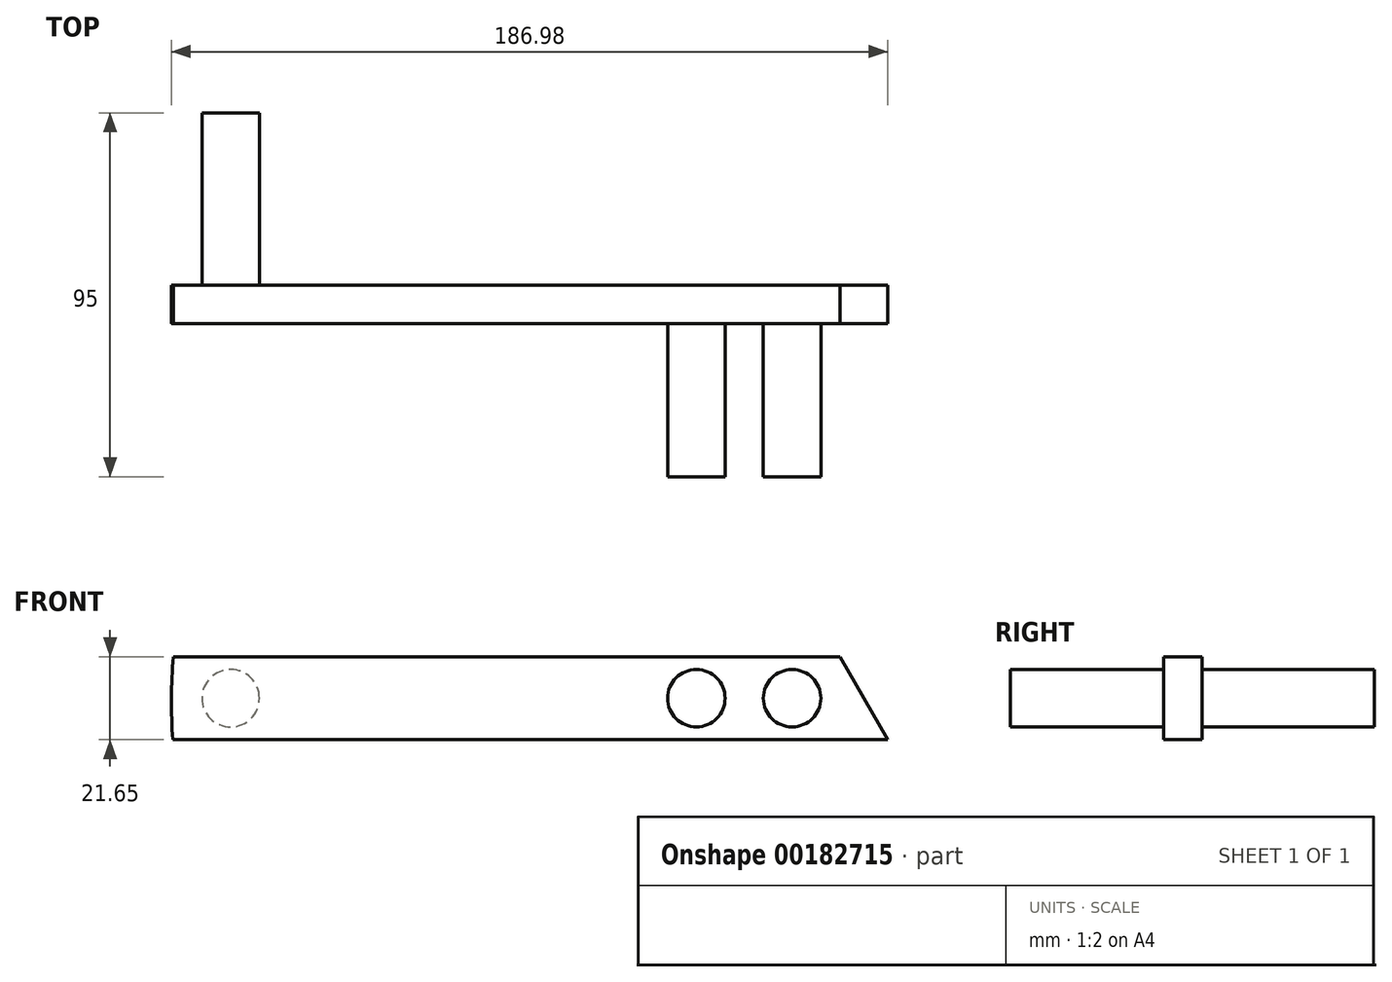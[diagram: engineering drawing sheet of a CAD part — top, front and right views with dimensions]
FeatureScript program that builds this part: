
annotation { "Feature Type Name" : "Feature", "Feature Type Description" : "" }
export const myFeature = defineFeature(function(context is Context, id is Id, definition is map)
    precondition{}
    {
        {
            var Q0;
            Q0=qCreatedBy(makeId("Front.planeOp"),FACE);
            var sketch = newSketch(context, id + "F0", { "sketchPlane" : qUnion([Q0])});
            skLineSegment(sketch, "E0", {"start": v(-38.02, -9.92) * mm, "end": v(-25.52, 11.73) * mm});
            skLineSegment(sketch, "E1", {"start": v(24.48, 11.73) * mm, "end": v(-25.52, 11.73) * mm});
            skLineSegment(sketch, "E2", {"start": v(36.98, -9.92) * mm, "end": v(24.48, 11.73) * mm});
            skLineSegment(sketch, "E3", {"start": v(36.98, -9.92) * mm, "end": v(-13.02, -9.92) * mm});
            skLineSegment(sketch, "E4", {"start": v(36.98, -9.92) * mm, "end": v(-38.02, -9.92) * mm});
            skLineSegment(sketch, "E5", {"start": v(11.98, -9.92) * mm, "end": v(11.98, -9.46) * mm});
            skLineSegment(sketch, "E6.trimOffspring", {"start": v(11.98, 11.26) * mm, "end": v(11.98, 11.73) * mm});
            skPoint(sketch, "E7", {"position": v(11.98, 0.9) * mm});
            skPoint(sketch, "E8", {"position": v(-13.02, 0.9) * mm});
            skPoint(sketch, "E9.orphan", {"position": v(-31.77, 0.9) * mm});
            skPoint(sketch, "E10.orphan", {"position": v(-13.02, 11.73) * mm});
            skCircle(sketch, "E11", {"center": v(-13.02, 0.9) * mm, "radius": 7.5 * mm});
            skCircle(sketch, "E12", {"center": v(11.98, 0.9) * mm, "radius": 7.5 * mm});
            skLineSegment(sketch, "E13", {"start": v(0, 0) * mm, "end": v(0, -9.92) * mm});
            skPoint(sketch, "E14", {"position": v(0, -9.92) * mm});
            skCircle(sketch, "E15", {"center": v(0, 0) * mm, "radius": 120 * mm});
            skLineSegment(sketch, "E16", {"start": v(36.98, -9.92) * mm, "end": v(-119.59, -9.92) * mm});
            skLineSegment(sketch, "E17", {"start": v(24.48, 11.73) * mm, "end": v(-119.43, 11.73) * mm});
            skCircle(sketch, "E18", {"center": v(0, 0) * mm, "radius": 150 * mm});
            skLineSegment(sketch, "E19", {"start": v(-119.43, 11.73) * mm, "end": v(-149.54, 11.73) * mm});
            skLineSegment(sketch, "E20", {"start": v(-119.59, -9.92) * mm, "end": v(-149.67, -9.92) * mm});
            skPoint(sketch, "E21", {"position": v(-134.56, 0.9) * mm});
            skCircle(sketch, "E22", {"center": v(-134.56, 0.9) * mm, "radius": 7.5 * mm});
            skSolve(sketch);
        }
        {
            var Q0;
            {var subQ2=sQuery(id+"F0.wireOp",EDGE,"E0");Q0=makeQuery(id+"F0.imprint","IMPRINT",FACE,{"disambiguationData":[TD([[makeQuery(id+"F0.imprint","IMPRINT",EDGE,{"derivedFrom":subQ2}),-1.0]])]});}
            var Q1;
            {var subQ0=sQuery(id+"F0.wireOp",EDGE,"E0");Q1=makeQuery(id+"F0.imprint","IMPRINT",FACE,{"disambiguationData":[TD([[makeQuery(id+"F0.imprint","IMPRINT",EDGE,{"derivedFrom":subQ0}),1.0]])]});}
            var Q2;
            {var subQ2=sQuery(id+"F0.wireOp",EDGE,"E19");Q2=makeQuery(id+"F0.imprint","IMPRINT",FACE,{"disambiguationData":[TD([[makeQuery(id+"F0.imprint","IMPRINT",EDGE,{"derivedFrom":subQ2}),1.0]])]});}
            var Q3;
            Q3=makeQuery(id+"F0.imprint","IMPRINT",FACE,{"disambiguationData":[TD([[makeQuery(id+"F0.imprint","IMPRINT",EDGE,{"derivedFrom":sQuery(id+"F0.wireOp",EDGE,"E22")}),1.0]])]});
            extrude(context, id + "F1", {"entities" : qUnion([Q0, Q1, Q2, Q3]), "depth" : 10 * mm});
        }
        {
            var Q0;
            Q0=makeQuery(id+"F0.imprint","IMPRINT",FACE,{"disambiguationData":[TD([[makeQuery(id+"F0.imprint","IMPRINT",EDGE,{"derivedFrom":sQuery(id+"F0.wireOp",EDGE,"E11")}),1.0]])]});
            var Q1;
            Q1=makeQuery(id+"F0.imprint","IMPRINT",FACE,{"disambiguationData":[TD([[makeQuery(id+"F0.imprint","IMPRINT",EDGE,{"derivedFrom":sQuery(id+"F0.wireOp",EDGE,"E12")}),1.0]])]});
            extrude(context, id + "F2", {"entities" : qUnion([Q0, Q1]), "operationType" : NewBodyOperationType.ADD, "depth" : 50 * mm});
        }
        {
            var Q0;
            Q0=makeQuery(id+"F0.imprint","IMPRINT",FACE,{"disambiguationData":[TD([[makeQuery(id+"F0.imprint","IMPRINT",EDGE,{"derivedFrom":sQuery(id+"F0.wireOp",EDGE,"E22")}),1.0]])]});
            extrude(context, id + "F3", {"entities" : qUnion([Q0]), "operationType" : NewBodyOperationType.ADD, "oppositeDirection" : true, "depth" : 45 * mm});
        }
    });
